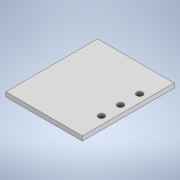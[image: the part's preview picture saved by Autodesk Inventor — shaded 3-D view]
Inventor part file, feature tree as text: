
AUTODESK INVENTOR PART (.ipt)
format: ipt  version: 2020.2 (Build 242310000, 310)  size: 99,328 bytes
history: native  units: in
note: dims shown in document units (in); Inventor stores cm internally (conversion verified against a paired STEP export)
features: extrude x1, sketch x1
ambient origin geometry x8: Origin, YZ Plane, XZ Plane, XY Plane, X Axis, Y Axis, Z Axis, Center Point
bodies: Solid1 (feature_tree)
feature tree (2):
  extrude  "Extrusion1"  Depth=2.3622in
  sketch  "Sketch1"  dims[d0=1.9685in d1=2.3622in d2=0.1575in d3=0.1575in d4=0.1575in d5=0.1181in d6=0.0in]
